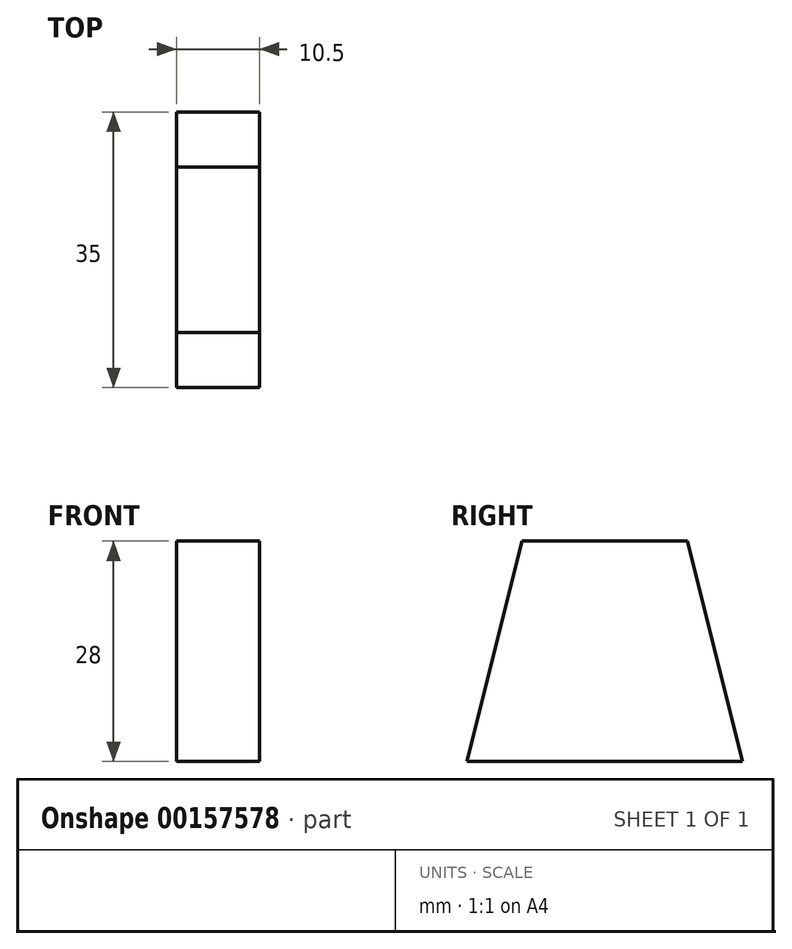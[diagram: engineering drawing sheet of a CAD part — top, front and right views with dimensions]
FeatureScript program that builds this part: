
annotation { "Feature Type Name" : "Feature", "Feature Type Description" : "" }
export const myFeature = defineFeature(function(context is Context, id is Id, definition is map)
    precondition{}
    {
        {
            var Q0;
            Q0=qCreatedBy(makeId("Top.planeOp"),FACE);
            var sketch = newSketch(context, id + "F0", { "sketchPlane" : qUnion([Q0])});
            skLineSegment(sketch, "E0.bottom", {"start": v(5.25, 10.5) * mm, "end": v(-5.25, 10.5) * mm});
            skLineSegment(sketch, "E0.top", {"start": v(5.25, -10.5) * mm, "end": v(-5.25, -10.5) * mm});
            skLineSegment(sketch, "E0.left", {"start": v(5.25, 10.5) * mm, "end": v(5.25, -10.5) * mm});
            skLineSegment(sketch, "E0.right", {"start": v(-5.25, 10.5) * mm, "end": v(-5.25, -10.5) * mm});
            skPoint(sketch, "E0.middle", {"position": v(0, 0) * mm});
            skSolve(sketch);
        }
        {
            var Q0;
            Q0=qCreatedBy(makeId("Top.planeOp"),FACE);
            cPlane(context, id + "F1", {"entities" : qUnion([Q0]), "cplaneType" : CPlaneType.OFFSET, "offset" : 28 * mm, "oppositeDirection" : true, "width" : 150 * mm, "height" : 150 * mm});
        }
        {
            var Q0;
            Q0=qCreatedBy(id+"F1.planeOp",FACE);
            var sketch = newSketch(context, id + "F2", { "sketchPlane" : qUnion([Q0])});
            skLineSegment(sketch, "E1.bottom", {"start": v(5.25, 17.5) * mm, "end": v(-5.25, 17.5) * mm});
            skLineSegment(sketch, "E1.top", {"start": v(5.25, -17.5) * mm, "end": v(-5.25, -17.5) * mm});
            skLineSegment(sketch, "E1.left", {"start": v(5.25, 17.5) * mm, "end": v(5.25, -17.5) * mm});
            skLineSegment(sketch, "E1.right", {"start": v(-5.25, 17.5) * mm, "end": v(-5.25, -17.5) * mm});
            skPoint(sketch, "E1.middle", {"position": v(0, 0) * mm});
            skSolve(sketch);
        }
        {
            var Q0;
            Q0=qSketchRegion(id+"F0",true);
            var Q1;
            Q1=qSketchRegion(id+"F2",true);
            loft(context, id + "F3", {"sheetProfilesArray" : [{ "sheetProfileEntities" : qUnion([Q0]) }, { "sheetProfileEntities" : qUnion([Q1]) }]});
        }
    });
